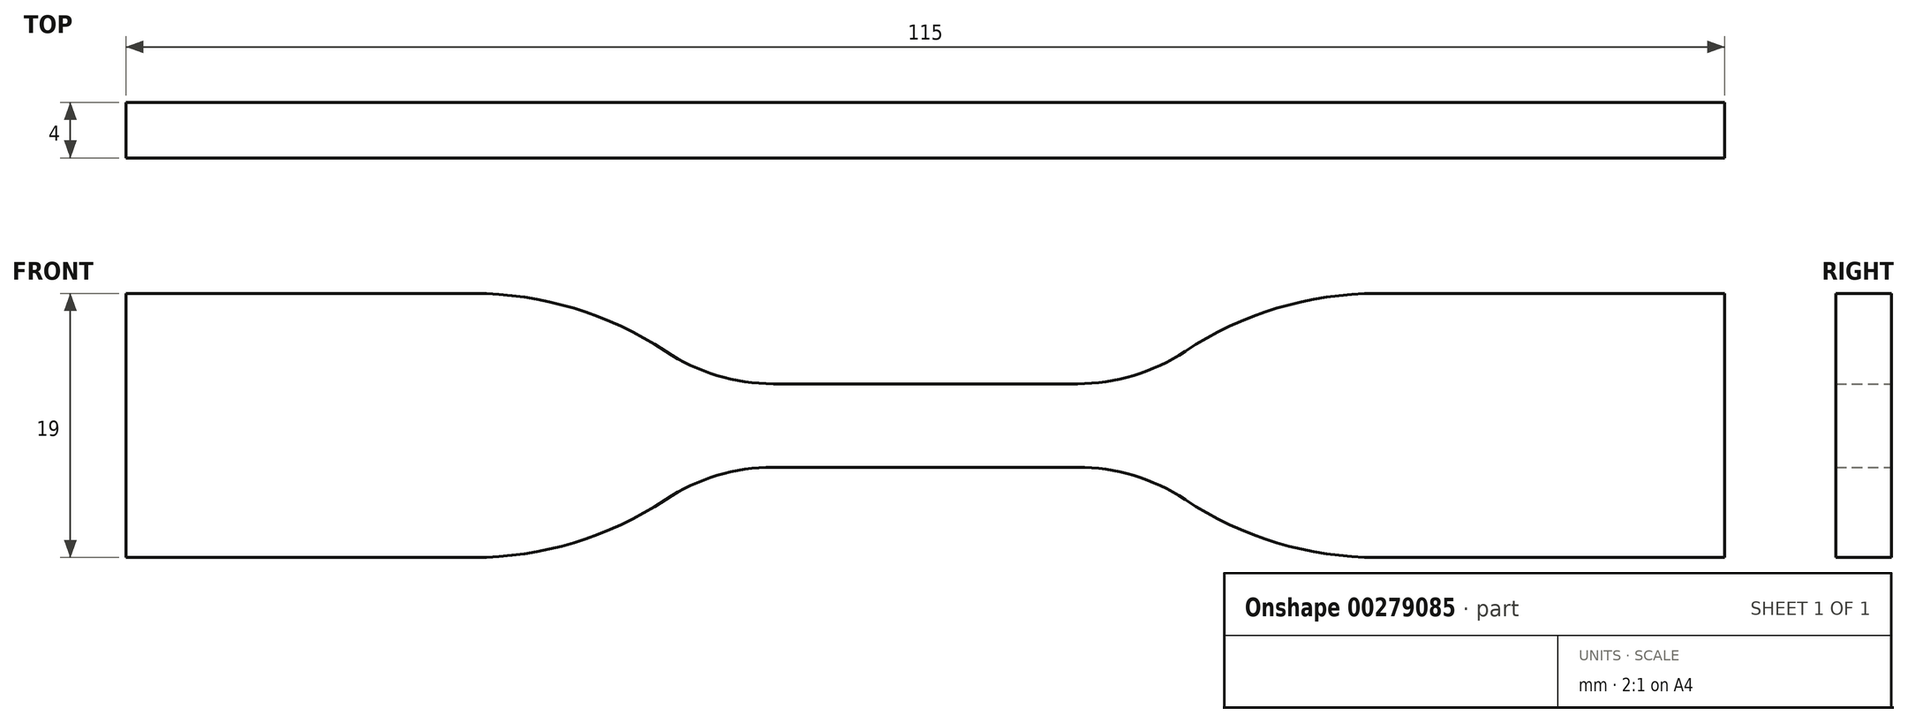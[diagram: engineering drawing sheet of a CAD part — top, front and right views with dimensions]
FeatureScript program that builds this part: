
annotation { "Feature Type Name" : "Feature", "Feature Type Description" : "" }
export const myFeature = defineFeature(function(context is Context, id is Id, definition is map)
    precondition{}
    {
        {
            var Q0;
            Q0=qCreatedBy(makeId("Front.planeOp"),FACE);
            var sketch = newSketch(context, id + "F0", { "sketchPlane" : qUnion([Q0])});
            skLineSegment(sketch, "E0", {"start": v(0, 3) * mm, "end": v(10.94, 3) * mm});
            skArc(sketch, "E1", {"start": v(10.94, 3) * mm, "mid": v(14.98, 3.6) * mm, "end": v(18.68, 5.33) * mm});
            skArc(sketch, "E2", {"start": v(32.5, 9.5) * mm, "mid": v(25.28, 8.44) * mm, "end": v(18.68, 5.33) * mm});
            skLineSegment(sketch, "E3", {"start": v(32.5, 9.5) * mm, "end": v(57.5, 9.5) * mm});
            skLineSegment(sketch, "E4.MirrorCS", {"start": v(32.5, -9.5) * mm, "end": v(57.5, -9.5) * mm});
            skLineSegment(sketch, "E5.MirrorCS", {"start": v(0, -3) * mm, "end": v(10.94, -3) * mm});
            skArc(sketch, "E6.MirrorCS", {"start": v(32.5, -9.5) * mm, "mid": v(25.28, -8.44) * mm, "end": v(18.68, -5.33) * mm});
            skArc(sketch, "E7.MirrorCS", {"start": v(10.94, -3) * mm, "mid": v(14.98, -3.6) * mm, "end": v(18.68, -5.33) * mm});
            skArc(sketch, "E8.MirrorCS", {"start": v(-10.94, -3) * mm, "mid": v(-14.98, -3.6) * mm, "end": v(-18.68, -5.33) * mm});
            skArc(sketch, "E9.MirrorCS", {"start": v(-32.5, -9.5) * mm, "mid": v(-25.28, -8.44) * mm, "end": v(-18.68, -5.33) * mm});
            skArc(sketch, "E10.MirrorCS", {"start": v(-32.5, 9.5) * mm, "mid": v(-25.28, 8.44) * mm, "end": v(-18.68, 5.33) * mm});
            skArc(sketch, "E11.MirrorCS", {"start": v(-10.94, 3) * mm, "mid": v(-14.98, 3.6) * mm, "end": v(-18.68, 5.33) * mm});
            skLineSegment(sketch, "E12.MirrorCS", {"start": v(0, -3) * mm, "end": v(-10.94, -3) * mm});
            skLineSegment(sketch, "E13.MirrorCS", {"start": v(0, 3) * mm, "end": v(-10.94, 3) * mm});
            skLineSegment(sketch, "E14.MirrorCS", {"start": v(-32.5, 9.5) * mm, "end": v(-57.5, 9.5) * mm});
            skLineSegment(sketch, "E15.MirrorCS", {"start": v(-32.5, -9.5) * mm, "end": v(-57.5, -9.5) * mm});
            skLineSegment(sketch, "E16", {"start": v(-57.5, 9.5) * mm, "end": v(-57.5, -9.5) * mm});
            skLineSegment(sketch, "E17", {"start": v(57.5, 9.5) * mm, "end": v(57.5, -9.5) * mm});
            skSolve(sketch);
        }
        {
            var Q0;
            Q0=makeQuery(id+"F0.imprint","IMPRINT",FACE,{"disambiguationData":[TD([[makeQuery(id+"F0.imprint","IMPRINT",EDGE,{"derivedFrom":sQuery(id+"F0.wireOp",EDGE,"E0")}),-1.0]])]});
            extrude(context, id + "F1", {"entities" : qUnion([Q0]), "endBound" : BoundingType.SYMMETRIC, "depth" : 4 * mm});
        }
    });
